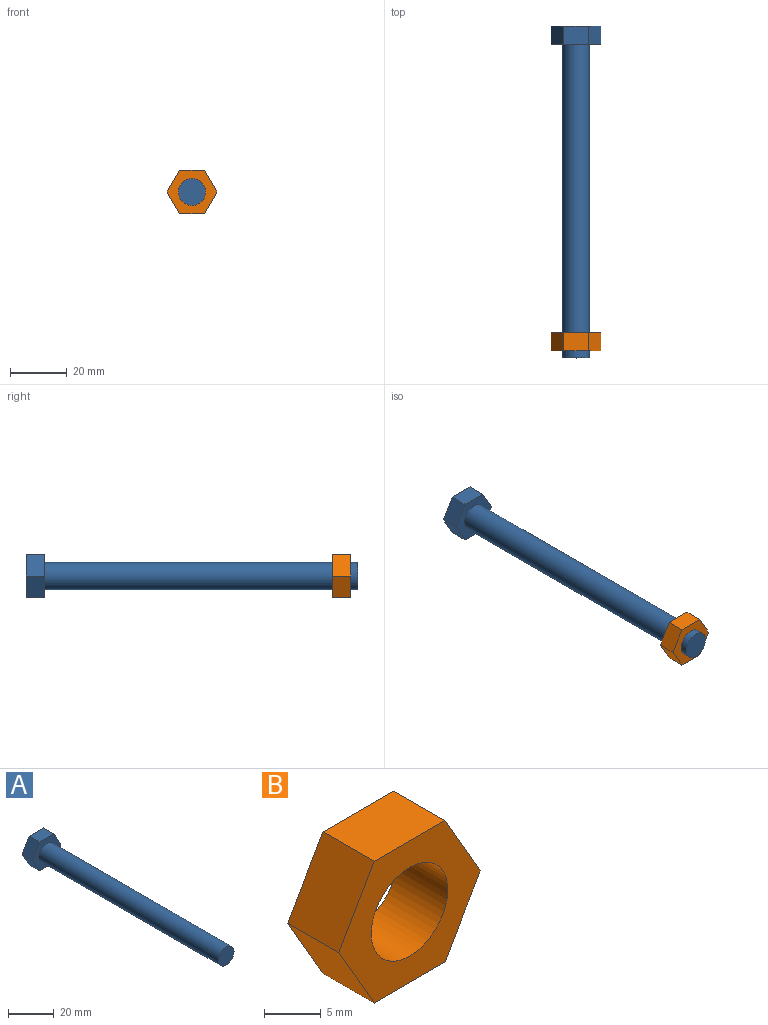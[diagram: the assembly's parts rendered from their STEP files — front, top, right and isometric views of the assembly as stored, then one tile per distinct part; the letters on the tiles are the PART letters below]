
ASSEMBLY  parts=2 mates=1
PART A: 10 faces, bbox 17.6x116.8x15.2 mm
  f0: cylinder r=4.76mm len=110.49mm, axis (0,-1,0), area 3306.3mm2, adj f1,f9
  f1: plane 9.53x9.53mm, normal (0,-1,0), area 71.3mm2, adj f0
  f2: plane 7.62x6.35mm, normal (-0.87,0,0.5), area 55.9mm2, adj f3,f7,f8,f9
  f3: plane 8.8x6.35mm, normal (0,0,1), area 55.9mm2, adj f2,f4,f8,f9
  f4: plane 7.62x6.35mm, normal (0.87,0,0.5), area 55.9mm2, adj f3,f5,f8,f9
  f5: plane 7.62x6.35mm, normal (0.87,0,-0.5), area 55.9mm2, adj f4,f6,f8,f9
  f6: plane 8.8x6.35mm, normal (0,0,-1), area 55.9mm2, adj f5,f7,f8,f9
  f7: plane 7.62x6.35mm, normal (-0.87,0,-0.5), area 55.9mm2, adj f2,f6,f8,f9
  f8: plane 17.6x15.24mm, normal (0,1,0), area 201.1mm2, adj f2,f3,f4,f5,f6,f7
  f9: plane 17.6x15.24mm, normal (0,-1,0), area 129.9mm2, adj f0,f2,f3,f4,f5,f6,f7
PART B: 9 faces, bbox 17.6x6.4x15.2 mm
  f0: plane 7.62x6.35mm, normal (0.87,0,0.5), area 55.9mm2, adj f1,f5,f6,f7
  f1: plane 8.8x6.35mm, normal (0,0,1), area 55.9mm2, adj f0,f2,f6,f7
  f2: plane 7.62x6.35mm, normal (-0.87,0,0.5), area 55.9mm2, adj f1,f3,f6,f7
  f3: plane 7.62x6.35mm, normal (-0.87,0,-0.5), area 55.9mm2, adj f2,f4,f6,f7
  f4: plane 8.8x6.35mm, normal (0,0,-1), area 55.9mm2, adj f3,f5,f6,f7
  f5: plane 7.62x6.35mm, normal (0.87,0,-0.5), area 55.9mm2, adj f0,f4,f6,f7
  f6: plane 17.6x15.24mm, normal (0,-1,0), area 129.9mm2, adj f0,f1,f2,f3,f4,f5,f8
  f7: plane 17.6x15.24mm, normal (0,1,0), area 129.9mm2, adj f0,f1,f2,f3,f4,f5,f8
  f8: cylinder r=4.76mm len=9.53mm, axis (0,1,0), area 190mm2, adj f6,f7
PLACE A t=(0,44.45,0)mm
PLACE B t=(0,-1.91,0)mm
MATE revolute A.f0 <-> B.f8  axis (0,-1,0) through (0,99.7,0)mm
